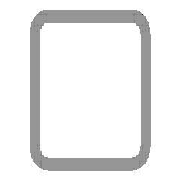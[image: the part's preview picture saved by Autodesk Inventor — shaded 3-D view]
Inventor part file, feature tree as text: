
AUTODESK INVENTOR PART (.ipt)
format: ipt  version: 2025 (Build 290162010, 162A)  size: 134,656 bytes
history: native  units: mm (DEFAULTED — no unit token found)
features: other x4, sketch x1, plane x1
ambient origin geometry x8: Origin, YZ Plane, XZ Plane, XY Plane, X Axis, Y Axis, Z Axis, Center Point
bodies: Solid1 (feature_tree), Body (feature_tree)
feature tree (6):
  parser-record x1  (decoder bookkeeping rows leaked as tree rows — omitted from the tree; the rows remain in map.json)
  other  "Driven Length"
  other  "Start Plane"
  other  "End Plane"
  sketch  "Sketch3"  dims[d3=580.0mm d4=0.0mm d7=6.0mm d9=80.0mm d11=80.0mm d12=3.0mm d13=40.0mm d14=620.0mm d15=40.0mm d16=40.0mm d17=90.0deg d18=580.0mm]
  plane  "Work Plane3"
